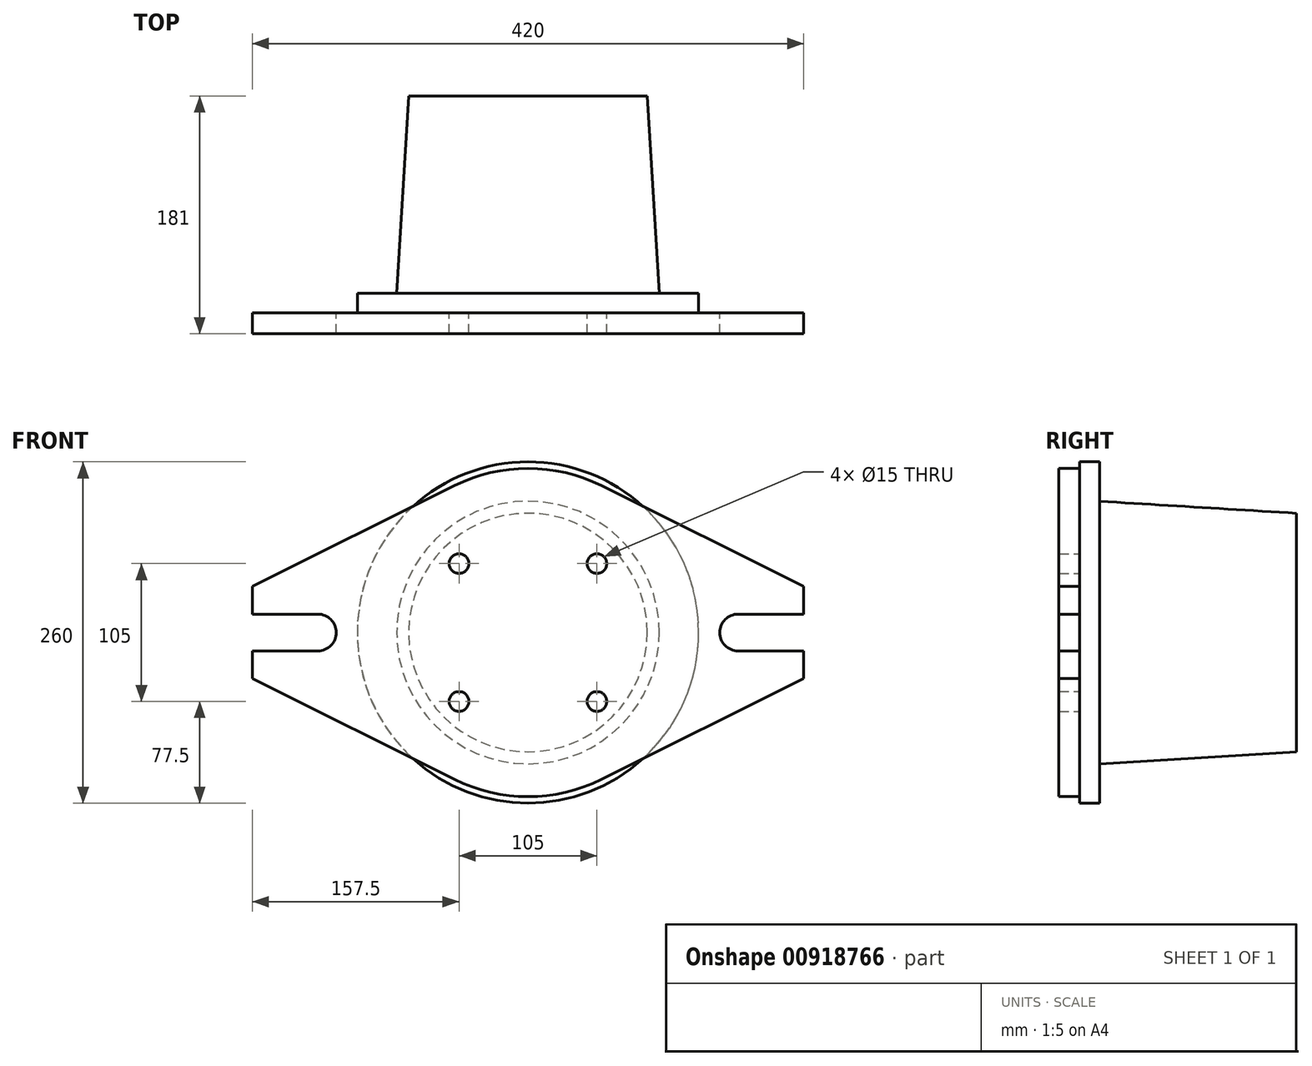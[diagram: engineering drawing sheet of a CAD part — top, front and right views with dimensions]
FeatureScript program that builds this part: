
annotation { "Feature Type Name" : "Feature", "Feature Type Description" : "" }
export const myFeature = defineFeature(function(context is Context, id is Id, definition is map)
    precondition{}
    {
        {
            var Q0;
            Q0=qCreatedBy(makeId("Front.planeOp"),FACE);
            var sketch = newSketch(context, id + "F0", { "sketchPlane" : qUnion([Q0])});
            skArc(sketch, "E0", {"start": v(-55.76, -111.87) * mm, "mid": v(0, -125) * mm, "end": v(55.76, -111.87) * mm});
            skLineSegment(sketch, "E1", {"start": v(-372.46, 0) * mm, "end": v(389.07, 0) * mm, "construction": true});
            skLineSegment(sketch, "E2", {"start": v(0, 226.74) * mm, "end": v(0, -139.67) * mm, "construction": true});
            skLineSegment(sketch, "E3", {"start": v(-210, -14) * mm, "end": v(-210, -35) * mm});
            skLineSegment(sketch, "E4", {"start": v(-210, -35) * mm, "end": v(-55.76, -111.87) * mm});
            skLineSegment(sketch, "E5.MirrorCS", {"start": v(210, -14) * mm, "end": v(210, -35) * mm});
            skLineSegment(sketch, "E6.MirrorCS", {"start": v(210, -35) * mm, "end": v(55.76, -111.87) * mm});
            skLineSegment(sketch, "E7.MirrorCS", {"start": v(-210, 14) * mm, "end": v(-210, 35) * mm});
            skLineSegment(sketch, "E8.MirrorCS", {"start": v(-210, 35) * mm, "end": v(-55.76, 111.87) * mm});
            skArc(sketch, "E9.MirrorCS", {"start": v(-55.76, 111.87) * mm, "mid": v(0, 125) * mm, "end": v(55.76, 111.87) * mm});
            skLineSegment(sketch, "E10.MirrorCS", {"start": v(210, 35) * mm, "end": v(55.76, 111.87) * mm});
            skLineSegment(sketch, "E11.MirrorCS", {"start": v(210, 14) * mm, "end": v(210, 35) * mm});
            skArc(sketch, "E12", {"start": v(-160, -14) * mm, "mid": v(-146, 0) * mm, "end": v(-160, 14) * mm});
            skLineSegment(sketch, "E13", {"start": v(-210, -14) * mm, "end": v(-160, -14) * mm});
            skLineSegment(sketch, "E14.MirrorCS", {"start": v(-210, 14) * mm, "end": v(-160, 14) * mm});
            skPoint(sketch, "E15.orphan", {"position": v(-210, 0) * mm});
            skLineSegment(sketch, "E16.MirrorCS", {"start": v(210, 14) * mm, "end": v(160, 14) * mm});
            skPoint(sketch, "E17.MirrorP", {"position": v(210, 0) * mm});
            skArc(sketch, "E18.MirrorCS", {"start": v(160, -14) * mm, "mid": v(146, 0) * mm, "end": v(160, 14) * mm});
            skLineSegment(sketch, "E19.MirrorCS", {"start": v(210, -14) * mm, "end": v(160, -14) * mm});
            skCircle(sketch, "E20", {"center": v(52.5, -52.5) * mm, "radius": 7.5 * mm});
            skCircle(sketch, "E21.MirrorC", {"center": v(52.5, 52.5) * mm, "radius": 7.5 * mm});
            skCircle(sketch, "E22.MirrorC", {"center": v(-52.5, -52.5) * mm, "radius": 7.5 * mm});
            skCircle(sketch, "E23.MirrorC", {"center": v(-52.5, 52.5) * mm, "radius": 7.5 * mm});
            skSolve(sketch);
        }
        {
            var Q0;
            Q0 = qSketchRegion(id + "F0", true);
            extrude(context, id + "F1", {"entities" : qUnion([Q0]), "depth" : 16 * mm, "offsetDistance" : 25 * mm});
        }
        {
            var Q0;
            Q0=makeQuery(id+"F1.opExtrude","CAP_FACE",FACE,{"disambiguationData":[OSD([sQuery(id+"F0.wireOp",EDGE,"E0"),sQuery(id+"F0.wireOp",EDGE,"E3"),sQuery(id+"F0.wireOp",EDGE,"E4"),sQuery(id+"F0.wireOp",EDGE,"E5.MirrorCS"),sQuery(id+"F0.wireOp",EDGE,"E6.MirrorCS"),sQuery(id+"F0.wireOp",EDGE,"E7.MirrorCS"),sQuery(id+"F0.wireOp",EDGE,"E8.MirrorCS"),sQuery(id+"F0.wireOp",EDGE,"E9.MirrorCS"),sQuery(id+"F0.wireOp",EDGE,"E10.MirrorCS"),sQuery(id+"F0.wireOp",EDGE,"E11.MirrorCS"),sQuery(id+"F0.wireOp",EDGE,"E12"),sQuery(id+"F0.wireOp",EDGE,"E13"),sQuery(id+"F0.wireOp",EDGE,"E14.MirrorCS"),sQuery(id+"F0.wireOp",EDGE,"E16.MirrorCS"),sQuery(id+"F0.wireOp",EDGE,"E18.MirrorCS"),sQuery(id+"F0.wireOp",EDGE,"E19.MirrorCS")])],"isStart":true});
            var sketch = newSketch(context, id + "F2", { "sketchPlane" : qUnion([Q0])});
            skCircle(sketch, "E24", {"center": v(0, 0) * mm, "radius": 130 * mm});
            skSolve(sketch);
        }
        {
            var Q0;
            Q0 = qSketchRegion(id + "F2", true);
            extrude(context, id + "F3", {"entities" : qUnion([Q0]), "depth" : 15 * mm, "offsetDistance" : 25 * mm});
        }
        {
            var Q0;
            Q0=makeQuery(id+"F3.opExtrude","CAP_FACE",FACE,{"disambiguationData":[OSD([sQuery(id+"F2.wireOp",EDGE,"E24")])],"isStart":false});
            var sketch = newSketch(context, id + "F4", { "sketchPlane" : qUnion([Q0])});
            skCircle(sketch, "E25", {"center": v(0, 0) * mm, "radius": 100 * mm});
            skSolve(sketch);
        }
        {
            var Q0;
            Q0 = qSketchRegion(id + "F4", true);
            extrude(context, id + "F5", {"entities" : qUnion([Q0]), "operationType" : NewBodyOperationType.ADD, "depth" : 150 * mm, "offsetDistance" : 25 * mm, "hasDraft" : true, "draftAngle" : 3.5 * degree, "draftPullDirection" : true});
        }
    });
